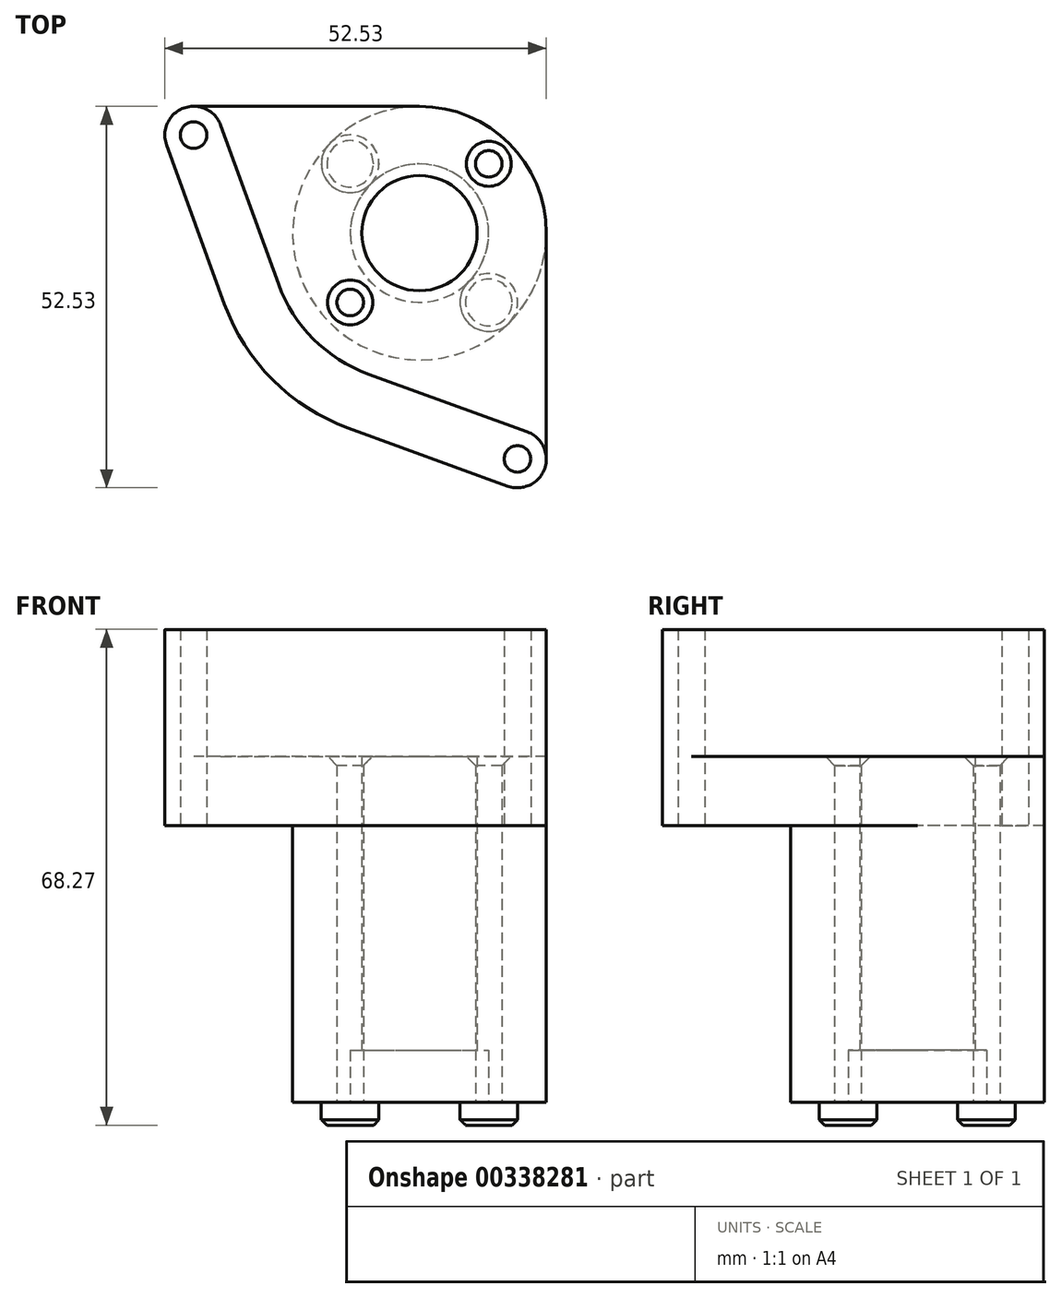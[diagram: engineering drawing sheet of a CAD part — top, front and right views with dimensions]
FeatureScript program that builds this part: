
annotation { "Feature Type Name" : "Feature", "Feature Type Description" : "" }
export const myFeature = defineFeature(function(context is Context, id is Id, definition is map)
    precondition{}
    {
        {
            var Q0;
            Q0=qCreatedBy(makeId("Top.planeOp"),FACE);
            var sketch = newSketch(context, id + "F0", { "sketchPlane" : qUnion([Q0])});
            skCircle(sketch, "E0", {"center": v(0, 0) * mm, "radius": 7.94 * mm});
            skCircle(sketch, "E1", {"center": v(0, 0) * mm, "radius": 17.46 * mm});
            skCircle(sketch, "E2", {"center": v(0, 0) * mm, "radius": 9.53 * mm, "construction": true});
            skLineSegment(sketch, "E3", {"start": v(0, 0) * mm, "end": v(9.54, 9.54) * mm, "construction": true});
            skLineSegment(sketch, "E4", {"start": v(9.54, 9.54) * mm, "end": v(9.54, 0) * mm, "construction": true});
            skLineSegment(sketch, "E5", {"start": v(9.54, 0) * mm, "end": v(0, 0) * mm, "construction": true});
            skCircle(sketch, "E6", {"center": v(9.54, 9.54) * mm, "radius": 3.97 * mm, "construction": true});
            skLineSegment(sketch, "E7", {"start": v(0, 0) * mm, "end": v(-9.54, -9.54) * mm, "construction": true});
            skCircle(sketch, "E8", {"center": v(9.54, 9.54) * mm, "radius": 1.83 * mm});
            skCircle(sketch, "E9", {"center": v(-9.54, -9.54) * mm, "radius": 1.83 * mm});
            skSolve(sketch);
        }
        {
            var Q0;
            Q0 = qSketchRegion(id + "F0", true);
            extrude(context, id + "F1", {"entities" : qUnion([Q0]), "depth" : 38.1 * mm});
        }
        {
            var Q0;
            Q0=makeQuery(id+"F1.opExtrude","CAP_FACE",FACE,{"disambiguationData":[OSD([sQuery(id+"F0.wireOp",EDGE,"E0"),sQuery(id+"F0.wireOp",EDGE,"E1")])],"isStart":false});
            var sketch = newSketch(context, id + "F2", { "sketchPlane" : qUnion([Q0])});
            skLineSegment(sketch, "E10", {"start": v(17.46, 0) * mm, "end": v(17.46, -31.1) * mm});
            skLineSegment(sketch, "E11", {"start": v(0, 17.46) * mm, "end": v(-31.1, 17.46) * mm});
            skArc(sketch, "E12", {"start": v(-31.1, 17.46) * mm, "mid": v(-34.35, 15.77) * mm, "end": v(-34.83, 12.14) * mm});
            skArc(sketch, "E13", {"start": v(12.14, -34.83) * mm, "mid": v(15.77, -34.35) * mm, "end": v(17.46, -31.1) * mm});
            skCircle(sketch, "E14", {"center": v(-31.1, 13.5) * mm, "radius": 1.83 * mm});
            skCircle(sketch, "E15", {"center": v(13.5, -31.1) * mm, "radius": 1.83 * mm});
            skCircle(sketch, "E16", {"center": v(0, 0) * mm, "radius": 7.94 * mm});
            skLineSegment(sketch, "E17", {"start": v(-34.83, 12.14) * mm, "end": v(-26.85, -9.77) * mm});
            skLineSegment(sketch, "E18", {"start": v(-26.85, -9.77) * mm, "end": v(-26.85, 1.18) * mm, "construction": true});
            skLineSegment(sketch, "E19", {"start": v(-26.85, 1.18) * mm, "end": v(-30.84, 1.18) * mm, "construction": true});
            skLineSegment(sketch, "E20", {"start": v(12.14, -34.83) * mm, "end": v(-9.77, -26.85) * mm});
            skArc(sketch, "E21", {"start": v(-26.85, -9.77) * mm, "mid": v(-20.2, -20.2) * mm, "end": v(-9.77, -26.85) * mm});
            skSolve(sketch);
        }
        {
            var Q0;
            {var subQ1=sQuery(id+"F2.wireOp",EDGE,"E10");Q0=makeQuery(id+"F2.imprint","IMPRINT",FACE,{"disambiguationData":[TD([[makeQuery(id+"F2.imprint","IMPRINT",EDGE,{"derivedFrom":subQ1}),-1.0]])]});}
            var Q1;
            Q1=makeQuery(id+"F2.imprint","IMPRINT",FACE,{"disambiguationData":[TD([[makeQuery(id+"F2.imprint","IMPRINT",EDGE,{"derivedFrom":sQuery(id+"F2.wireOp",EDGE,"E16")}),-1.0]])]});
            extrude(context, id + "F3", {"entities" : qUnion([Q0, Q1]), "operationType" : NewBodyOperationType.ADD, "depth" : 9.52 * mm});
        }
        {
            var Q0;
            Q0=makeQuery(id+"F3.opExtrude","CAP_FACE",FACE,{"disambiguationData":[OSD([sQuery(id+"F0.wireOp",EDGE,"E1"),sQuery(id+"F2.wireOp",EDGE,"E10"),sQuery(id+"F2.wireOp",EDGE,"E11"),sQuery(id+"F2.wireOp",EDGE,"E12"),sQuery(id+"F2.wireOp",EDGE,"E13"),sQuery(id+"F2.wireOp",EDGE,"X8qrc68y-sert-XPDv-yaph-47fqzMAi9iMU"),sQuery(id+"F2.wireOp",EDGE,"E14"),sQuery(id+"F2.wireOp",EDGE,"E15"),sQuery(id+"F2.wireOp",EDGE,"E16")])],"isStart":false});
            var sketch = newSketch(context, id + "F4", { "sketchPlane" : qUnion([Q0])});
            skArc(sketch, "E22", {"start": v(-26.85, -9.77) * mm, "mid": v(-20.2, -20.2) * mm, "end": v(-9.77, -26.85) * mm});
            skArc(sketch, "E23", {"start": v(-19.4, -7.06) * mm, "mid": v(-14.6, -14.6) * mm, "end": v(-7.06, -19.4) * mm});
            skLineSegment(sketch, "E24", {"start": v(-26.85, -9.77) * mm, "end": v(-34.83, 12.14) * mm});
            skArc(sketch, "E25", {"start": v(-27.37, 14.85) * mm, "mid": v(-32.45, 17.22) * mm, "end": v(-34.83, 12.14) * mm});
            skLineSegment(sketch, "E26", {"start": v(-27.37, 14.85) * mm, "end": v(-19.4, -7.06) * mm});
            skLineSegment(sketch, "E27", {"start": v(-7.06, -19.4) * mm, "end": v(14.85, -27.37) * mm});
            skArc(sketch, "E28", {"start": v(12.14, -34.83) * mm, "mid": v(17.22, -32.45) * mm, "end": v(14.85, -27.37) * mm});
            skLineSegment(sketch, "E29", {"start": v(-9.77, -26.85) * mm, "end": v(12.14, -34.83) * mm});
            skCircle(sketch, "E30", {"center": v(13.5, -31.1) * mm, "radius": 1.83 * mm});
            skCircle(sketch, "E31", {"center": v(-31.1, 13.5) * mm, "radius": 1.83 * mm});
            skSolve(sketch);
        }
        {
            var Q0;
            Q0 = qSketchRegion(id + "F4", true);
            extrude(context, id + "F5", {"entities" : qUnion([Q0]), "operationType" : NewBodyOperationType.ADD, "depth" : 17.46 * mm});
        }
        {
            var Q0;
            Q0=makeQuery(id+"F1.opExtrude","CAP_FACE",FACE,{"disambiguationData":[OSD([sQuery(id+"F0.wireOp",EDGE,"E0"),sQuery(id+"F0.wireOp",EDGE,"E1")])],"isStart":true});
            var sketch = newSketch(context, id + "F6", { "sketchPlane" : qUnion([Q0])});
            skCircle(sketch, "E32", {"center": v(0, 0) * mm, "radius": 9.53 * mm});
            skSolve(sketch);
        }
        {
            var Q0;
            Q0 = qSketchRegion(id + "F6", true);
            extrude(context, id + "F7", {"entities" : qUnion([Q0]), "operationType" : NewBodyOperationType.REMOVE, "oppositeDirection" : true, "depth" : 7.14 * mm});
        }
        {
            var Q0;
            Q0=makeQuery(id+"F1.opExtrude","CAP_FACE",FACE,{"disambiguationData":[OSD([sQuery(id+"F0.wireOp",EDGE,"E0"),sQuery(id+"F0.wireOp",EDGE,"E1"),sQuery(id+"F0.wireOp",EDGE,"E8"),sQuery(id+"F0.wireOp",EDGE,"E9")])],"isStart":true});
            var sketch = newSketch(context, id + "F8", { "sketchPlane" : qUnion([Q0])});
            skLineSegment(sketch, "E33", {"start": v(0, -17.46) * mm, "end": v(-9.54, -17.46) * mm, "construction": true});
            skLineSegment(sketch, "E34", {"start": v(-9.54, -17.46) * mm, "end": v(-9.54, -9.54) * mm, "construction": true});
            skCircle(sketch, "E35", {"center": v(-9.54, -9.54) * mm, "radius": 3.97 * mm});
            skLineSegment(sketch, "E36", {"start": v(17.46, 0) * mm, "end": v(17.46, 9.54) * mm, "construction": true});
            skLineSegment(sketch, "E37", {"start": v(17.46, 9.54) * mm, "end": v(9.54, 9.54) * mm, "construction": true});
            skCircle(sketch, "E38", {"center": v(9.54, 9.54) * mm, "radius": 3.97 * mm});
            skLineSegment(sketch, "E39", {"start": v(9.54, 9.54) * mm, "end": v(-9.54, -9.54) * mm, "construction": true});
            skLineSegment(sketch, "E40", {"start": v(9.54, -9.54) * mm, "end": v(0, 0) * mm, "construction": true});
            skLineSegment(sketch, "E41", {"start": v(0, 0) * mm, "end": v(-9.54, 9.54) * mm, "construction": true});
            skSolve(sketch);
        }
        {
            var Q0;
            Q0 = qSketchRegion(id + "F8", true);
            extrude(context, id + "F9", {"entities" : qUnion([Q0]), "operationType" : NewBodyOperationType.ADD, "depth" : 3.17 * mm});
        }
        {
            var Q0;
            Q0=makeQuery(id+"F9.opExtrude","CAP_EDGE",EDGE,{"disambiguationData":[OSD([sQuery(id+"F8.wireOp",EDGE,"E38")])],"isStart":false});
            var Q1;
            Q1=makeQuery(id+"F9.opExtrude","CAP_EDGE",EDGE,{"disambiguationData":[OSD([sQuery(id+"F8.wireOp",EDGE,"E35")])],"isStart":false});
            chamfer(context, id + "F10", {"entities" : qUnion([Q0, Q1]), "width" : 0.76 * mm, "tangentPropagation" : true});
        }
        {
            var Q0;
            Q0=makeQuery(id+"F3.opExtrude","CAP_EDGE",EDGE,{"disambiguationData":[OSD([sQuery(id+"F0.wireOp",EDGE,"E8")])],"isStart":false});
            var Q1;
            Q1=makeQuery(id+"F3.opExtrude","CAP_EDGE",EDGE,{"disambiguationData":[OSD([sQuery(id+"F0.wireOp",EDGE,"E9")])],"isStart":false});
            chamfer(context, id + "F11", {"entities" : qUnion([Q0, Q1]), "chamferType" : ChamferType.OFFSET_ANGLE, "width" : 1.27 * mm, "oppositeDirection" : false, "angle" : 45 * degree, "tangentPropagation" : true});
        }
    });
